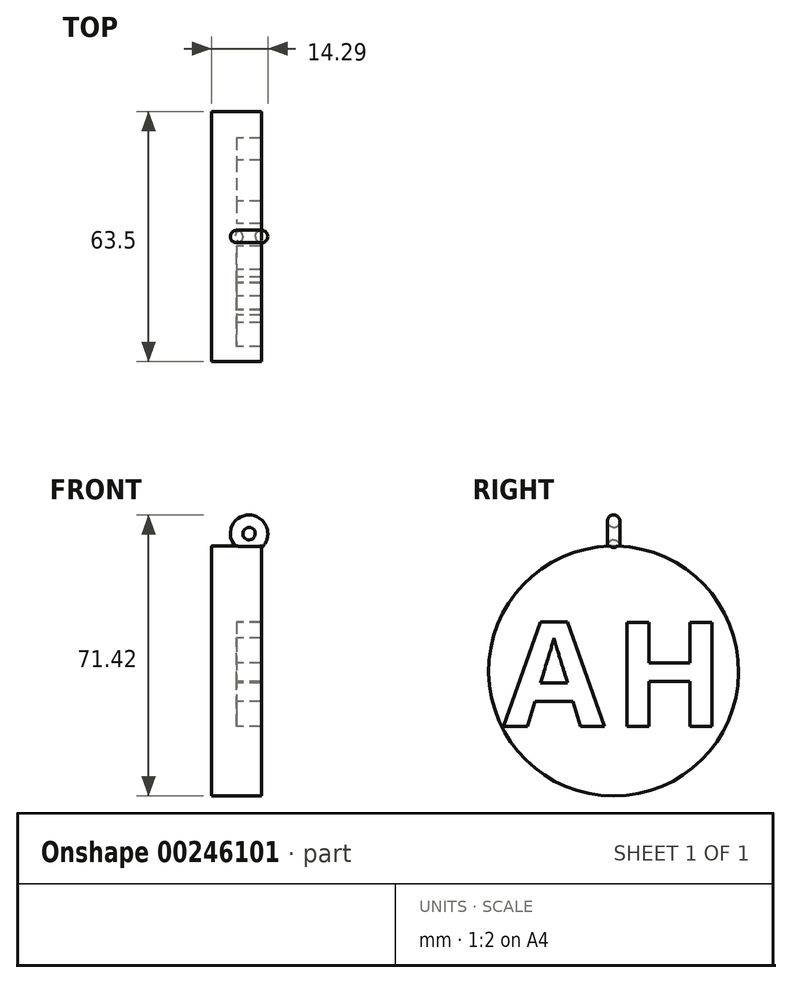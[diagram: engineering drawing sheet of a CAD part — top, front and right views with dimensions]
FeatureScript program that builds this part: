
annotation { "Feature Type Name" : "Feature", "Feature Type Description" : "" }
export const myFeature = defineFeature(function(context is Context, id is Id, definition is map)
    precondition{}
    {
        {
            var Q0;
            Q0=qCreatedBy(makeId("Right.planeOp"),FACE);
            var sketch = newSketch(context, id + "F0", { "sketchPlane" : qUnion([Q0])});
            skCircle(sketch, "E0", {"center": v(0, 0) * mm, "radius": 31.75 * mm});
            skSolve(sketch);
        }
        {
            var Q0;
            Q0=qCreatedBy(makeId("Right.planeOp"),FACE);
            var sketch = newSketch(context, id + "F1", { "sketchPlane" : qUnion([Q0])});
            skCircle(sketch, "E1", {"center": v(0, 0) * mm, "radius": 31.75 * mm});
            skText(sketch, "E2", { "text": "A", "fontName": "OpenSans-Bold.ttf"});
            skText(sketch, "E3", { "text": "H", "fontName": "OpenSans-Bold.ttf"});
            const initialGuessF1  = {"E2": [-0.02796, -0.01404, 1, 0, 0.02667], "E3": [0, -0.01404, 1, 0, 0.02668]};
            skSetInitialGuess(sketch, initialGuessF1);
            skSolve(sketch);
        }
        {
            var Q0;
            Q0 = qSketchRegion(id + "F1", true);
            extrude(context, id + "F2", {"entities" : qUnion([Q0]), "depth" : 6.35 * mm});
        }
        {
            var Q0;
            Q0 = qSketchRegion(id + "F0", true);
            extrude(context, id + "F3", {"entities" : qUnion([Q0]), "operationType" : NewBodyOperationType.ADD, "oppositeDirection" : true, "depth" : 6.35 * mm});
        }
        {
            var Q0;
            Q0=makeQuery(id+"F1.imprint","IMPRINT",FACE,{"disambiguationData":[TD([[makeQuery(id+"F1.imprint","IMPRINT",EDGE,{"derivedFrom":sQuery(id+"F1.wireOp",EDGE,"E2.sketch_text.stroke-8")}),1.0]])]});
            extrude(context, id + "F4", {"entities" : qUnion([Q0]), "operationType" : NewBodyOperationType.ADD, "depth" : 6.35 * mm});
        }
        {
            var Q0;
            Q0=qCreatedBy(makeId("Right.planeOp"),FACE);
            cPlane(context, id + "F5", {"entities" : qUnion([Q0]), "cplaneType" : CPlaneType.OFFSET, "offset" : 3.17 * mm, "width" : 152.4 * mm, "height" : 152.4 * mm});
        }
        {
            var Q0;
            Q0=qCreatedBy(id+"F5.planeOp",FACE);
            var sketch = newSketch(context, id + "F6", { "sketchPlane" : qUnion([Q0])});
            skCircle(sketch, "E4", {"center": v(0, 31.74) * mm, "radius": 1.59 * mm});
            skLineSegment(sketch, "E5", {"start": v(0, 31.74) * mm, "end": v(0, 34.91) * mm});
            skLineSegment(sketch, "E6", {"start": v(0, 34.91) * mm, "end": v(-20.42, 34.91) * mm});
            skSolve(sketch);
        }
        {
            var Q0;
            Q0 = qSketchRegion(id + "F6", true);
            var Q1;
            Q1=sQuery(id+"F6.wireOp",EDGE,"E6");
            revolve(context, id + "F7", {"operationType" : NewBodyOperationType.ADD, "entities" : qUnion([Q0]), "axis" : qUnion([Q1]), "revolveType" : RevolveType.FULL});
        }
    });
